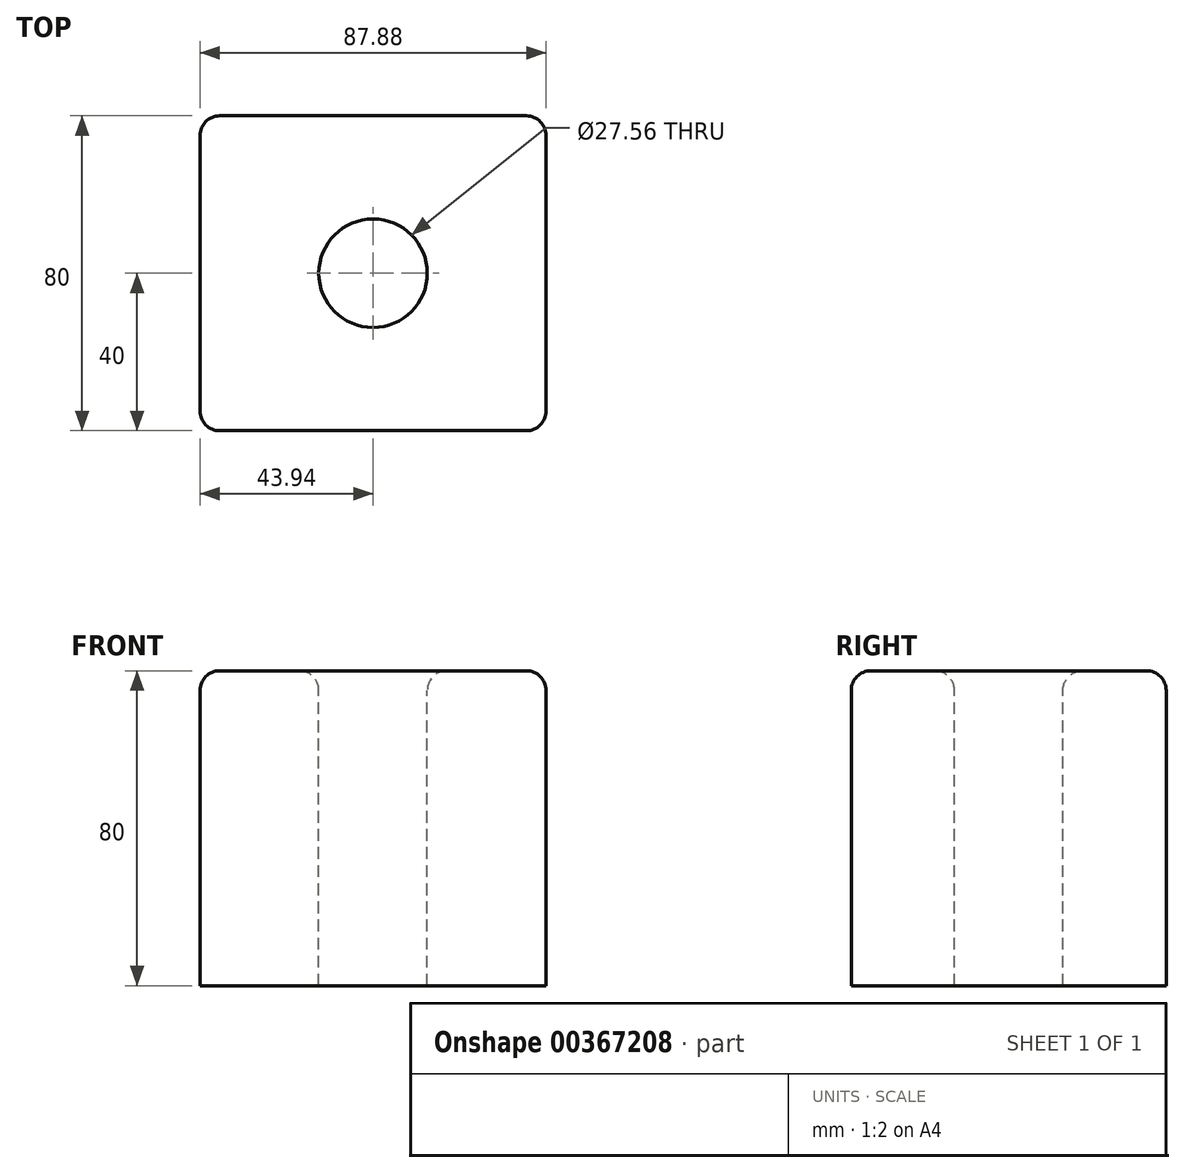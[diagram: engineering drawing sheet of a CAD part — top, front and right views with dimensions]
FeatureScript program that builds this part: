
annotation { "Feature Type Name" : "Feature", "Feature Type Description" : "" }
export const myFeature = defineFeature(function(context is Context, id is Id, definition is map)
    precondition{}
    {
        {
            var Q0;
            Q0=qCreatedBy(makeId("Top.planeOp"),FACE);
            var sketch = newSketch(context, id + "F0", { "sketchPlane" : qUnion([Q0])});
            skLineSegment(sketch, "E0.bottom", {"start": v(-43.94, 40) * mm, "end": v(43.94, 40) * mm});
            skLineSegment(sketch, "E0.top", {"start": v(-43.94, -40) * mm, "end": v(43.94, -40) * mm});
            skLineSegment(sketch, "E0.left", {"start": v(-43.94, 40) * mm, "end": v(-43.94, -40) * mm});
            skLineSegment(sketch, "E0.right", {"start": v(43.94, 40) * mm, "end": v(43.94, -40) * mm});
            skPoint(sketch, "E0.middle", {"position": v(0, 0) * mm});
            skSolve(sketch);
        }
        {
            var Q0;
            Q0=makeQuery(id+"F0.imprint","IMPRINT",FACE,{"disambiguationData":[TD([[makeQuery(id+"F0.imprint","IMPRINT",EDGE,{"derivedFrom":sQuery(id+"F0.wireOp",EDGE,"E0.bottom")}),-1.0]])]});
            extrude(context, id + "F1", {"entities" : qUnion([Q0]), "depth" : 80 * mm});
        }
        {
            var Q0;
            Q0=makeQuery(id+"F1.opExtrude","CAP_FACE",FACE,{"disambiguationData":[OSD([sQuery(id+"F0.wireOp",EDGE,"E0.bottom"),sQuery(id+"F0.wireOp",EDGE,"E0.top"),sQuery(id+"F0.wireOp",EDGE,"E0.left"),sQuery(id+"F0.wireOp",EDGE,"E0.right")])],"isStart":false});
            var sketch = newSketch(context, id + "F2", { "sketchPlane" : qUnion([Q0])});
            skCircle(sketch, "E1", {"center": v(0, 0) * mm, "radius": 13.78 * mm});
            skSolve(sketch);
        }
        {
            var Q0;
            Q0=makeQuery(id+"F2.imprint","IMPRINT",FACE,{"disambiguationData":[TD([[makeQuery(id+"F2.imprint","IMPRINT",EDGE,{"derivedFrom":sQuery(id+"F2.wireOp",EDGE,"E1")}),1.0]])]});
            extrude(context, id + "F3", {"entities" : qUnion([Q0]), "operationType" : NewBodyOperationType.ADD, "depth" : 25 * mm});
        }
        {
            var Q0;
            Q0=makeQuery(id+"F3.opExtrude","CAP_FACE",FACE,{"disambiguationData":[OSD([sQuery(id+"F2.wireOp",EDGE,"E1")])],"isStart":false});
            var sketch = newSketch(context, id + "F4", { "sketchPlane" : qUnion([Q0])});
            skSolve(sketch);
        }
        {
            var Q0;
            Q0=makeQuery(id+"F4.imprint","IMPRINT",FACE,{"disambiguationData":[TD([[makeQuery(id+"F4.imprint","IMPRINT",EDGE,{"derivedFrom":makeQuery(id+"F3.opExtrude","CAP_EDGE",EDGE,{"disambiguationData":[OSD([sQuery(id+"F2.wireOp",EDGE,"E1")])],"isStart":false})}),1.0]])]});
            var sketch = newSketch(context, id + "F5", { "sketchPlane" : qUnion([Q0])});
            skSolve(sketch);
        }
        {
            var Q0;
            Q0=makeQuery(id+"F4.imprint","IMPRINT",FACE,{"disambiguationData":[TD([[makeQuery(id+"F4.imprint","IMPRINT",EDGE,{"derivedFrom":makeQuery(id+"F3.opExtrude","CAP_EDGE",EDGE,{"disambiguationData":[OSD([sQuery(id+"F2.wireOp",EDGE,"E1")])],"isStart":false})}),1.0]])]});
            var sketch = newSketch(context, id + "F6", { "sketchPlane" : qUnion([Q0])});
            skSolve(sketch);
        }
        {
            var Q0;
            Q0=makeQuery(id+"F4.imprint","IMPRINT",FACE,{"disambiguationData":[TD([[makeQuery(id+"F4.imprint","IMPRINT",EDGE,{"derivedFrom":makeQuery(id+"F3.opExtrude","CAP_EDGE",EDGE,{"disambiguationData":[OSD([sQuery(id+"F2.wireOp",EDGE,"E1")])],"isStart":false})}),1.0]])]});
            extrude(context, id + "F7", {"entities" : qUnion([Q0]), "operationType" : NewBodyOperationType.REMOVE, "oppositeDirection" : true, "depth" : 25 * mm});
        }
        {
            var Q0;
            Q0=makeQuery(id+"F5.imprint","IMPRINT",FACE,{"disambiguationData":[TD([[makeQuery(id+"F5.imprint","IMPRINT",EDGE,{"derivedFrom":makeQuery(id+"F4.imprint","IMPRINT",EDGE,{"derivedFrom":makeQuery(id+"F3.opExtrude","CAP_EDGE",EDGE,{"disambiguationData":[OSD([sQuery(id+"F2.wireOp",EDGE,"E1")])],"isStart":false})})}),1.0]])]});
            extrude(context, id + "F8", {"entities" : qUnion([Q0]), "operationType" : NewBodyOperationType.REMOVE, "oppositeDirection" : true, "depth" : 25 * mm});
        }
        {
            var Q0;
            Q0=makeQuery(id+"F6.imprint","IMPRINT",FACE,{"disambiguationData":[TD([[makeQuery(id+"F6.imprint","IMPRINT",EDGE,{"derivedFrom":makeQuery(id+"F4.imprint","IMPRINT",EDGE,{"derivedFrom":makeQuery(id+"F3.opExtrude","CAP_EDGE",EDGE,{"disambiguationData":[OSD([sQuery(id+"F2.wireOp",EDGE,"E1")])],"isStart":false})})}),1.0]])]});
            extrude(context, id + "F9", {"entities" : qUnion([Q0]), "operationType" : NewBodyOperationType.REMOVE, "endBound" : BoundingType.THROUGH_ALL, "oppositeDirection" : true, "depth" : 25 * mm});
        }
        {
            var Q0;
            Q0=makeQuery(id+"F7.boolean.opBoolean","MERGE",FACE,{"derivedFrom":[makeQuery(id+"F1.opExtrude","CAP_FACE",FACE,{"disambiguationData":[OSD([sQuery(id+"F0.wireOp",EDGE,"E0.bottom"),sQuery(id+"F0.wireOp",EDGE,"E0.top"),sQuery(id+"F0.wireOp",EDGE,"E0.left"),sQuery(id+"F0.wireOp",EDGE,"E0.right")])],"isStart":false}),makeQuery(id+"F7.opExtrude","CAP_FACE",FACE,{"disambiguationData":[OSD([sQuery(id+"F2.wireOp",EDGE,"E1")])],"isStart":false})]});
            fillet(context, id + "F10", {"entities" : qUnion([Q0]), "radius" : 5 * mm, "tangentPropagation" : true, "allowEdgeOverflow" : false});
        }
        {
            var Q0;
            Q0=makeQuery(id+"F10.opFillet","BLEND_FACE",FACE,{"disambiguationData":[OSD([sQuery(id+"F0.wireOp",EDGE,"E0.bottom")])]});
            var Q1;
            Q1=makeQuery(id+"F10.opFillet","BLEND_FACE",FACE,{"disambiguationData":[OSD([sQuery(id+"F0.wireOp",EDGE,"E0.right")])]});
            var Q2;
            {var subQ0=sQuery(id+"F0.wireOp",EDGE,"E0.top");Q2=makeQuery(id+"F10.opFillet","BLEND_EDGE",EDGE,{"blendedFrom":[makeQuery(id+"F1.opExtrude","CAP_EDGE",EDGE,{"disambiguationData":[OSD([subQ0])],"isStart":false}),makeQuery(id+"F7.boolean.opBoolean","MERGE",FACE,{"derivedFrom":[makeQuery(id+"F1.opExtrude","CAP_FACE",FACE,{"disambiguationData":[OSD([sQuery(id+"F0.wireOp",EDGE,"E0.bottom"),subQ0,sQuery(id+"F0.wireOp",EDGE,"E0.left"),sQuery(id+"F0.wireOp",EDGE,"E0.right")])],"isStart":false}),makeQuery(id+"F7.opExtrude","CAP_FACE",FACE,{"disambiguationData":[OSD([sQuery(id+"F2.wireOp",EDGE,"E1")])],"isStart":false})]})],"blendedInto":[makeQuery(id+"F7.boolean.opBoolean","MERGE",FACE,{"derivedFrom":[makeQuery(id+"F1.opExtrude","CAP_FACE",FACE,{"disambiguationData":[OSD([sQuery(id+"F0.wireOp",EDGE,"E0.bottom"),subQ0,sQuery(id+"F0.wireOp",EDGE,"E0.left"),sQuery(id+"F0.wireOp",EDGE,"E0.right")])],"isStart":false}),makeQuery(id+"F7.opExtrude","CAP_FACE",FACE,{"disambiguationData":[OSD([sQuery(id+"F2.wireOp",EDGE,"E1")])],"isStart":false})]})]});}
            var Q3;
            Q3=makeQuery(id+"F10.opFillet","BLEND_FACE",FACE,{"disambiguationData":[OSD([sQuery(id+"F0.wireOp",EDGE,"E0.left")])]});
            var Q4;
            Q4=makeQuery(id+"F10.opFillet","BLEND_FACE",FACE,{"disambiguationData":[OSD([sQuery(id+"F0.wireOp",EDGE,"E0.bottom"),sQuery(id+"F0.wireOp",EDGE,"E0.top"),sQuery(id+"F0.wireOp",EDGE,"E0.left"),sQuery(id+"F0.wireOp",EDGE,"E0.right"),sQuery(id+"F2.wireOp",EDGE,"E1")])]});
            fillet(context, id + "F11", {"entities" : qUnion([Q0, Q1, Q2, Q3, Q4]), "radius" : 5 * mm, "tangentPropagation" : true, "allowEdgeOverflow" : false});
        }
    });
